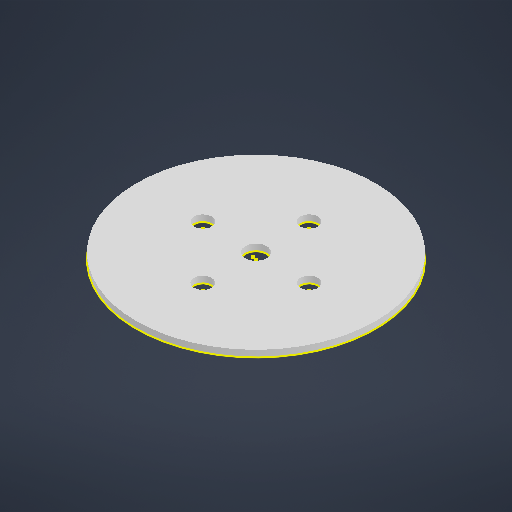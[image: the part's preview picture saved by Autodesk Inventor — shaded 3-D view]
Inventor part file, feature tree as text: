
AUTODESK INVENTOR PART (.ipt)
format: ipt  version: 2025.2 (Build 292293000, 293)  size: 222,720 bytes
history: native  units: in
note: dims shown in document units (in); Inventor stores cm internally (conversion verified against a paired STEP export)
features: sketch x2, other x2, extrude x1
ambient origin geometry x8: Origin, YZ Plane, XZ Plane, XY Plane, X Axis, Y Axis, Z Axis, Center Point
bodies: Solid1 (feature_tree)
feature tree (5):
  extrude  "Extrusion1"  Depth=0.2in
  sketch  "Sketch2"  dims[d2=0.0625in d3=0.0in]
  other  "A-Side Definition"
  sketch  "Sketch1"  dims[d0=2.25in d1=0.2in]
  other  "Definition1"
